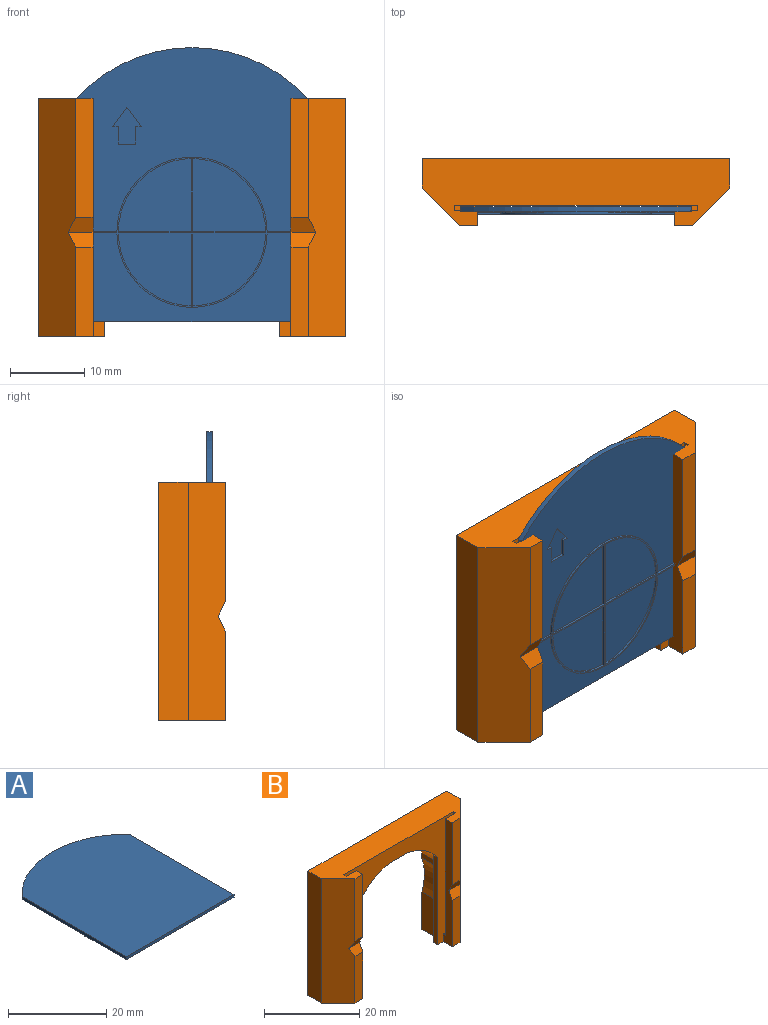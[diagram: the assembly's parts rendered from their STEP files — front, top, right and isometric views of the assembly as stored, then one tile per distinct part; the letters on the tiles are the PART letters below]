
ASSEMBLY  parts=2 mates=1
PART A: 40 faces, bbox 31x36.8x1 mm
  f0: plane 5.41x0.3mm, normal (0,-1,0), area 1.6mm2, adj f4,f13,f18,f35
  f1: plane 5.41x0.3mm, normal (0,1,0), area 1.6mm2, adj f2,f13,f18,f38
  f2: plane 31x24.71mm, normal (0,0,-1), area 532.3mm2, adj f1,f7,f11,f12,f13,f20,f21,f22
  f3: plane 9.8x9.79mm, normal (0,0,-1), area 75mm2, adj f9,f28,f37
  f4: plane 31x11.9mm, normal (0,0,-1), area 211mm2, adj f0,f6,f11,f13,f14,f35
  f5: plane 9.79x9.78mm, normal (0,0,-1), area 74.8mm2, adj f8,f31,f34
  f6: plane 5.41x0.3mm, normal (0,-1,0), area 1.6mm2, adj f4,f11,f18,f35
  f7: plane 5.41x0.3mm, normal (0,1,0), area 1.6mm2, adj f2,f11,f18,f38
  f8: plane 9.79x0.3mm, normal (0,-1,0), area 2.9mm2, adj f5,f18,f31,f34
  f9: plane 9.79x0.3mm, normal (0,1,0), area 2.9mm2, adj f3,f18,f28,f37
  f10: plane 9.8x9.79mm, normal (0,0,-1), area 75mm2, adj f19,f29,f39
  f11: plane 30x1mm, normal (1,0,0), area 21.1mm2, adj f2,f4,f6,f7,f12,f14,f15,f18
  f12: cylinder r=21.05mm len=31mm, axis (0,0,-1), area 24.4mm2, adj f2,f11,f13,f15
  f13: plane 30x1mm, normal (-1,0,0), area 21.1mm2, adj f0,f1,f2,f4,f12,f14,f15,f18
  f14: plane 31x0.7mm, normal (0,-1,0), area 21.7mm2, adj f4,f11,f13,f15
  f15: plane 36.81x31mm, normal (0,0,1), area 1076mm2, adj f11,f12,f13,f14
  f16: plane 9.79x9.78mm, normal (0,0,-1), area 74.8mm2, adj f17,f32,f36
  f17: plane 9.79x0.3mm, normal (0,-1,0), area 2.9mm2, adj f16,f18,f32,f36
  f18: plane 31x20.19mm, normal (0,0,-1), area 18.6mm2, adj f0,f1,f6,f7,f8,f9,f11,f13
  f19: plane 9.79x0.3mm, normal (0,1,0), area 2.9mm2, adj f10,f18,f29,f39
  f20: plane 2.33x0.4mm, normal (0,1,0), area 0.9mm2, adj f2,f21,f26,f27
  f21: plane 2.4x0.4mm, normal (-1,0,0), area 1mm2, adj f2,f20,f22,f27
  f22: plane 0.77x0.4mm, normal (0,1,0), area 0.3mm2, adj f2,f21,f23,f27
  f23: plane 2.58x1.94mm, normal (-0.8,-0.6,0), area 1.3mm2, adj f2,f22,f24,f27
  f24: plane 2.58x1.94mm, normal (0.8,-0.6,0), area 1.3mm2, adj f2,f23,f25,f27
  f25: plane 0.77x0.4mm, normal (0,1,0), area 0.3mm2, adj f2,f24,f26,f27
  f26: plane 2.4x0.4mm, normal (1,0,0), area 1mm2, adj f2,f20,f25,f27
  f27: plane 4.98x3.88mm, normal (0,0,-1), area 10.6mm2, adj f20,f21,f22,f23,f24,f25,f26
  f28: plane 9.8x0.3mm, normal (-1,0,0), area 2.9mm2, adj f3,f9,f30,f37
  f29: plane 9.8x0.3mm, normal (1,0,0), area 2.9mm2, adj f10,f19,f30,f39
  f30: plane 9.91x0.2mm, normal (0,0,-1), area 2mm2, adj f18,f28,f29
  f31: plane 9.78x0.3mm, normal (-1,0,0), area 2.9mm2, adj f5,f8,f33,f34
  f32: plane 9.78x0.3mm, normal (1,0,0), area 2.9mm2, adj f16,f17,f33,f36
  f33: plane 9.89x0.2mm, normal (0,0,-1), area 2mm2, adj f18,f31,f32
  f34: cylinder r=9.89mm len=9.79mm, axis (0,0,1), area 4.6mm2, adj f5,f8,f18,f31
  f35: cylinder r=10.09mm len=20.18mm, axis (0,0,1), area 9.4mm2, adj f0,f4,f6,f18
  f36: cylinder r=9.89mm len=9.79mm, axis (0,0,1), area 4.6mm2, adj f16,f17,f18,f32
  f37: cylinder r=9.89mm len=9.8mm, axis (0,0,1), area 4.6mm2, adj f3,f9,f18,f28
  f38: cylinder r=10.09mm len=20.18mm, axis (0,0,1), area 9.5mm2, adj f1,f2,f7,f18
  f39: cylinder r=9.89mm len=9.8mm, axis (0,0,1), area 4.6mm2, adj f10,f18,f19,f29
PART B: 38 faces, bbox 41.3x9x32 mm
  f0: plane 22.44x1.3mm, normal (1,0,0), area 29.2mm2, adj f12,f22,f25,f29
  f1: plane 6.3x5.43mm, normal (0,0,-1), area 34.2mm2, adj f7,f8,f12,f29
  f2: plane 5x1.3mm, normal (-1,0,0), area 6.5mm2, adj f7,f8,f10,f34
  f3: plane 9.63x5mm, normal (1,0,0), area 48.1mm2, adj f8,f22,f25,f35
  f4: plane 16x2.34mm, normal (0,-1,0), area 37.4mm2, adj f16,f17,f32,f37
  f5: plane 16x2.34mm, normal (0,-1,0), area 37.4mm2, adj f16,f26,f31,f36
  f6: plane 32x4mm, normal (-1,0,0), area 128mm2, adj f8,f16,f25,f36
  f7: cylinder r=14.46mm len=10.58mm, axis (0,1,0), area 85mm2, adj f1,f2,f8,f10,f11,f12
  f8: plane 41.28x32mm, normal (0,1,0), area 621.8mm2, adj f1,f2,f3,f6,f7,f9,f15,f16
  f9: plane 9.63x5mm, normal (-1,0,0), area 48.1mm2, adj f8,f10,f15,f34
  f10: plane 22.44x2.26mm, normal (0,1,0), area 37.1mm2, adj f2,f7,f9,f11,f15,f34
  f11: plane 22.44x1.3mm, normal (-1,0,0), area 29.2mm2, adj f7,f10,f12,f15
  f12: plane 32.6x32mm, normal (0,-1,0), area 406.3mm2, adj f0,f1,f7,f11,f13,f15,f16,f17
  f13: plane 30x0.7mm, normal (-1,0,0), area 21mm2, adj f12,f14,f16,f20
  f14: plane 30x3mm, normal (0,1,0), area 90mm2, adj f13,f16,f17,f20
  f15: plane 9x8.9mm, normal (0,0,-1), area 55.6mm2, adj f8,f9,f10,f11,f12,f17,f18,f19
  f16: plane 41.28x9mm, normal (0,0,1), area 270.5mm2, adj f4,f5,f6,f8,f12,f13,f14,f17
  f17: plane 32x2.7mm, normal (-1,0,0), area 63.4mm2, adj f4,f12,f14,f15,f16,f18,f20,f32
  f18: plane 12x2.34mm, normal (0,-1,0), area 28.1mm2, adj f15,f17,f33,f37
  f19: plane 32x4mm, normal (1,0,0), area 128mm2, adj f8,f15,f16,f37
  f20: plane 3x0.7mm, normal (0,0,1), area 2.1mm2, adj f12,f13,f14,f17
  f21: plane 5x1.3mm, normal (1,0,0), area 6.5mm2, adj f8,f22,f29,f35
  f22: plane 22.44x2.26mm, normal (0,1,0), area 37.1mm2, adj f0,f3,f21,f25,f29,f35
  f23: plane 30x0.7mm, normal (1,0,0), area 21mm2, adj f12,f16,f24,f28
  f24: plane 30x3mm, normal (0,1,0), area 90mm2, adj f16,f23,f26,f28
  f25: plane 9x8.9mm, normal (0,0,-1), area 55.6mm2, adj f0,f3,f6,f8,f12,f22,f26,f27
  f26: plane 32x2.7mm, normal (1,0,0), area 63.4mm2, adj f5,f12,f16,f24,f25,f27,f28,f30
  f27: plane 12x2.34mm, normal (0,-1,0), area 28.1mm2, adj f25,f26,f30,f36
  f28: plane 3x0.7mm, normal (0,0,1), area 2.1mm2, adj f12,f23,f24,f26
  f29: cylinder r=14.46mm len=10.58mm, axis (0,1,0), area 85mm2, adj f0,f1,f8,f12,f21,f22
  f30: plane 3.34x2mm, normal (0,-0.89,0.45), area 6.4mm2, adj f26,f27,f31,f36
  f31: plane 3.34x2mm, normal (0,-0.89,-0.45), area 6.4mm2, adj f5,f26,f30,f36
  f32: plane 3.34x2mm, normal (0,-0.89,-0.45), area 6.4mm2, adj f4,f17,f33,f37
  f33: plane 3.34x2mm, normal (0,-0.89,0.45), area 6.4mm2, adj f17,f18,f32,f37
  f34: cylinder r=14mm len=8.74mm, axis (0,-1,0), area 44.5mm2, adj f2,f8,f9,f10
  f35: cylinder r=14mm len=8.74mm, axis (0,-1,0), area 44.5mm2, adj f3,f8,f21,f22
  f36: plane 32x5mm, normal (-0.71,-0.71,0), area 223.4mm2, adj f5,f6,f16,f25,f27,f30,f31
  f37: plane 32x5mm, normal (0.71,-0.71,0), area 223.4mm2, adj f4,f15,f16,f18,f19,f32,f33
PLACE A rot(axis=(0,0.71,0.71),180deg) t=(12.45,0.71,-4.56)mm
PLACE B t=(12.45,7.91,-5.56)mm fixed
MATE slider A.f14 <-> B.f16  axis (0,0,-1) through (12.45,1.41,-17.56)mm
